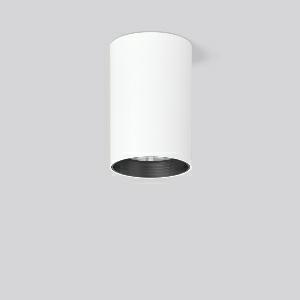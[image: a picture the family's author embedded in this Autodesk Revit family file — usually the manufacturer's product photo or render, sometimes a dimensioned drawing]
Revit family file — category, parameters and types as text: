
# Revit family: heledon_maxi_a_931242_002_d65a
name_source: partatom
category: Lighting Fixtures
units: mm (PartAtom-declared; Revit-internal decimal feet)

## family parameters
Cut with Voids When Loaded = No
Host = Face
Light Source = No
Part Type = Normal
Room Calculation Point = No
Round Connector Dimension = Use Diameter
Shared = No

## types (1)
- HELEDON maxi A (1 x LED Modul 920 meat+, 1850 lm, 2000)
    Apparent Load = 33 VA
    Approval mark = CE
    CIE Flux Codes = 96 99 100 100 100
    Color Rendering = 90
    Color Temperature = 2000
    Default Elevation = 1800 mm
    Description = Series: HELEDON maxi
Cylindrical surface-mounted downlight. Housing: die-cast aluminium, powder-coated. Internal ceiling frame polycarbonate with bayonet mounting. Black plastic ring and recessed LED to prevent glare from the side. Optical assembly with lens made of plastic (polycarbonate) for the best homogeneous light distribution - can be changed without tools. Special LED for illumination of meat included. Suitable for Ceiling mounting. Easy installation with a separate ceiling frame with bayonet mounting and plug connection. Driver integrated. Connected via plug-in connector. High quality converter without flickering and stroboscopic effect. The following accessories can be mounted without use of tools: interchangeable lenses, decorative glasses, honeycomb louvre, clear and frosted diffusers, white interchangeable plastic ring. 
Colour: traffic white, matt (RAL 9016)
Diameter: 123 mm
Height: 183 mm
Lamp: LED
Socket: without socket
Colour temperature: meat +
System power: 33 W
Rated luminous flux: 1850 lm
Luminous efficiency: 56 lm/W
Control gear: Regulated power supply
Protection class: I
Type of protection: IP 20
    Height = 183 mm
    Lamp = 1 x LED Modul 920 meat+
    Lamp Light Flux = 1850 lm
    Lamp count = 1
    Length = 123 mm
    Lifetime = 50000 h
    Luminous efficacy = 56 lm/W
    Manufacturer = RZB
    ModVariant = No
    Model = 931242.002
    Mounting Place = Ceiling
    Mounting Type = Surface mounted
    Number of Poles = 1
    OnlyDefault = Yes
    Power Factor = 1
    Product Name = HELEDON maxi A
    Product group = Surface mounted downlights
    ProductGroupID = 302
    Protection Class = Protection class I
    Protection Degree = IP 20
    RLX_Detail_Level = 1
    RLX_Emergency_Light_Flux = 0 lm
    RLX_Emergency_Type = 0
    RLX_Emergency_Type_DB = No
    RlxData = <blob elided: 98105 chars, md5=2024f785>
    Socket = socket
    Standby Power = 0 W
    System Light Flux = 1850 lm
    System Power = 33 W
    Type Comments = Product without accessories
    Type Image = 931193.002.jpg
    URL = http://relux.com
    VarID = ---
    Voltage = 230 V
    Voltage Range = 220-240 V
    Weight = 0.00 kg
    Width = 0 mm  [stored 0 ft]

note: [stored X ft] marks values corroborated as IEEE doubles in the binary element streams (Revit-internal decimal feet)

## geometry (parser evidence)
native form markers: Blend x4, Sweep x9
no freeform markers — native parametric forms only
